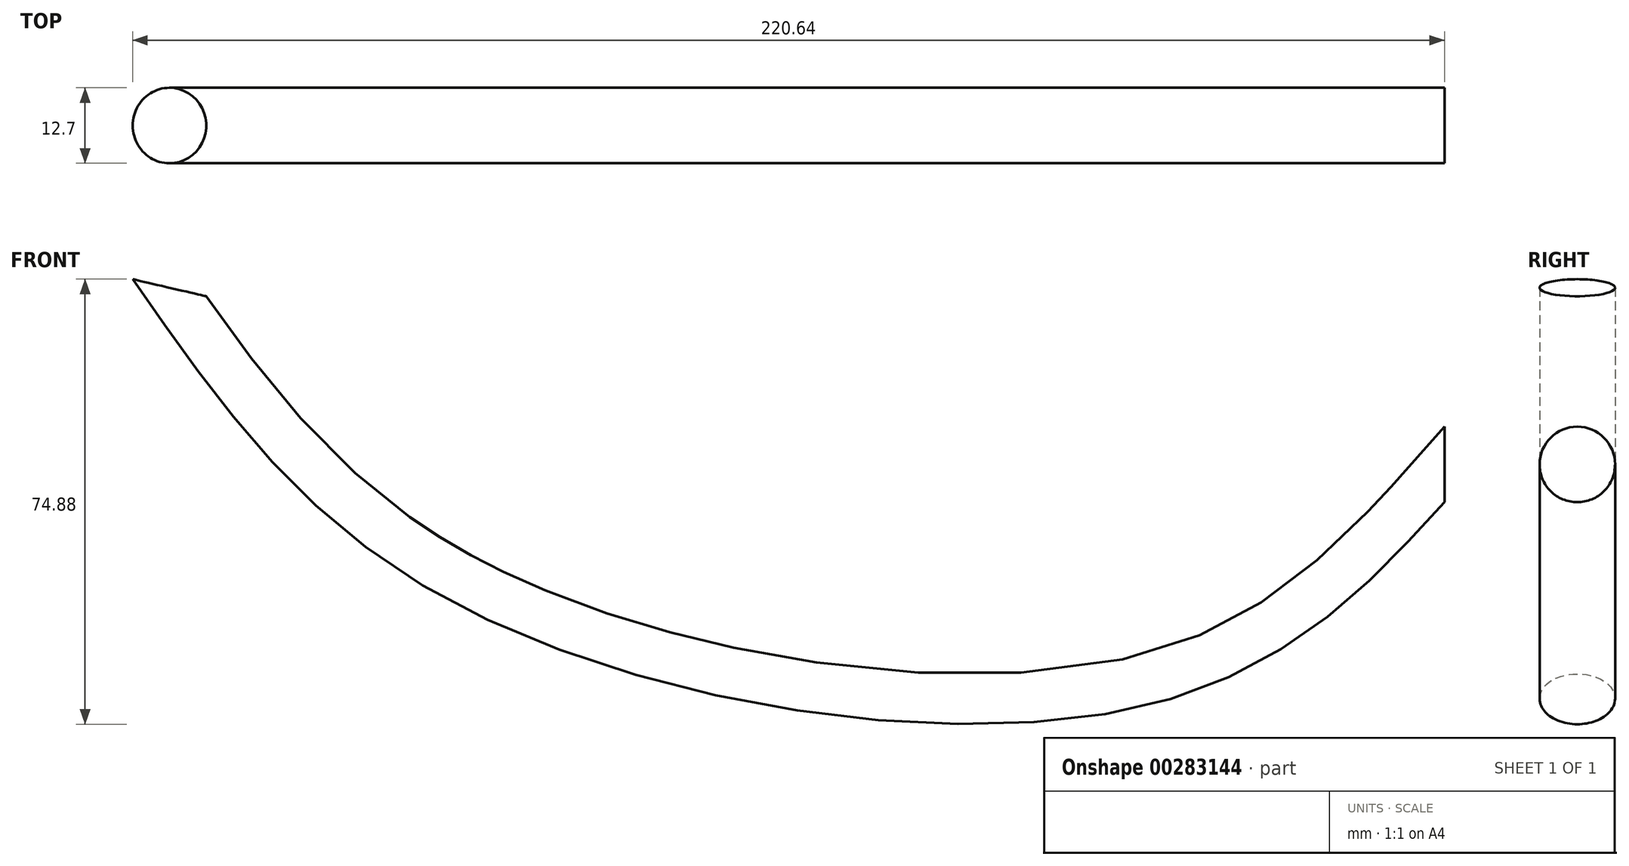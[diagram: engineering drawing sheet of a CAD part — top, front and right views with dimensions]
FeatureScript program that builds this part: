
annotation { "Feature Type Name" : "Feature", "Feature Type Description" : "" }
export const myFeature = defineFeature(function(context is Context, id is Id, definition is map)
    precondition{}
    {
        {
            var Q0;
            Q0=qCreatedBy(makeId("Front.planeOp"),FACE);
            var sketch = newSketch(context, id + "F0", { "sketchPlane" : qUnion([Q0])});
            skFitSpline(sketch, "E0", {"points": [v(0, 0) * mm, v(-50, -36.04) * mm, v(-164, -19.82) * mm, v(-214.46, 29.74) * mm], "startDerivative": vector(-137.5, -154.15) * mm, "endDerivative": vector(-124.2, 175.96) * mm});
            skSolve(sketch);
        }
        {
            var Q0;
            Q0=qCreatedBy(makeId("Right.planeOp"),FACE);
            var sketch = newSketch(context, id + "F1", { "sketchPlane" : qUnion([Q0])});
            skCircle(sketch, "E1", {"center": v(0, 0) * mm, "radius": 6.35 * mm});
            skSolve(sketch);
        }
        {
            var Q0;
            Q0=makeQuery(id+"F1.imprint","IMPRINT",FACE,{"disambiguationData":[TD([[makeQuery(id+"F1.imprint","IMPRINT",EDGE,{"derivedFrom":sQuery(id+"F1.wireOp",EDGE,"E1")}),1.0]])]});
            var Q1;
            Q1=sQuery(id+"F0.wireOp",EDGE,"E0");
            sweep(context, id + "F2", {"profiles" : qUnion([Q0]), "path" : qUnion([Q1])});
        }
    });
